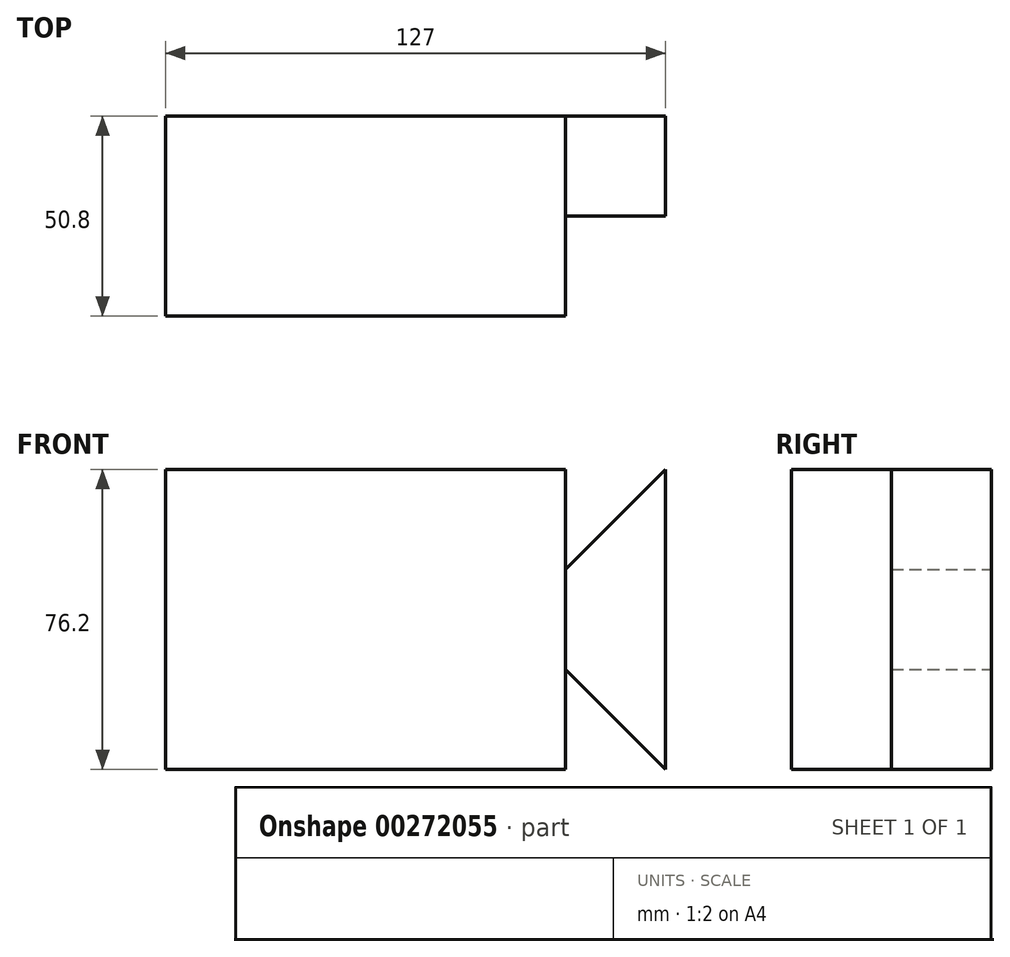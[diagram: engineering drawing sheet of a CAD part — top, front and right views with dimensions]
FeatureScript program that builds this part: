
annotation { "Feature Type Name" : "Feature", "Feature Type Description" : "" }
export const myFeature = defineFeature(function(context is Context, id is Id, definition is map)
    precondition{}
    {
        {
            var Q0;
            Q0=qCreatedBy(makeId("Front.planeOp"),FACE);
            var sketch = newSketch(context, id + "F0", { "sketchPlane" : qUnion([Q0])});
            skLineSegment(sketch, "E0.bottom", {"start": v(-50.8, 38.1) * mm, "end": v(50.8, 38.1) * mm});
            skLineSegment(sketch, "E0.top", {"start": v(-50.8, -38.1) * mm, "end": v(50.8, -38.1) * mm});
            skLineSegment(sketch, "E0.left", {"start": v(-50.8, 38.1) * mm, "end": v(-50.8, -38.1) * mm});
            skLineSegment(sketch, "E0.right", {"start": v(50.8, 38.1) * mm, "end": v(50.8, -38.1) * mm});
            skPoint(sketch, "E0.middle", {"position": v(0, 0) * mm});
            skSolve(sketch);
        }
        {
            var Q0;
            Q0 = qSketchRegion(id + "F0", true);
            extrude(context, id + "F1", {"entities" : qUnion([Q0]), "depth" : 50.8 * mm});
        }
        {
            var Q0;
            Q0=qCreatedBy(makeId("Front.planeOp"),FACE);
            var sketch = newSketch(context, id + "F2", { "sketchPlane" : qUnion([Q0])});
            skLineSegment(sketch, "E1.left", {"start": v(50.8, 12.7) * mm, "end": v(50.8, -12.7) * mm});
            skPoint(sketch, "E2", {"position": v(50.8, 0) * mm});
            skPoint(sketch, "E3.trimOffspring.start.orphan", {"position": v(76.2, -2.75) * mm});
            skLineSegment(sketch, "E4", {"start": v(76.2, -38.1) * mm, "end": v(76.2, 38.1) * mm});
            skPoint(sketch, "E5", {"position": v(76.2, 0) * mm});
            skLineSegment(sketch, "E6", {"start": v(50.8, 12.7) * mm, "end": v(76.2, 38.1) * mm});
            skLineSegment(sketch, "E7", {"start": v(50.8, -12.7) * mm, "end": v(76.2, -38.1) * mm});
            skSolve(sketch);
        }
        {
            var Q0;
            Q0 = qSketchRegion(id + "F2", true);
            extrude(context, id + "F3", {"entities" : qUnion([Q0]), "operationType" : NewBodyOperationType.ADD, "depth" : 25.4 * mm});
        }
        {
            var Q0;
            Q0 = qSketchRegion(id + "F2", true);
            extrude(context, id + "F4", {"entities" : qUnion([Q0]), "operationType" : NewBodyOperationType.ADD, "depth" : 25.4 * mm});
        }
    });
